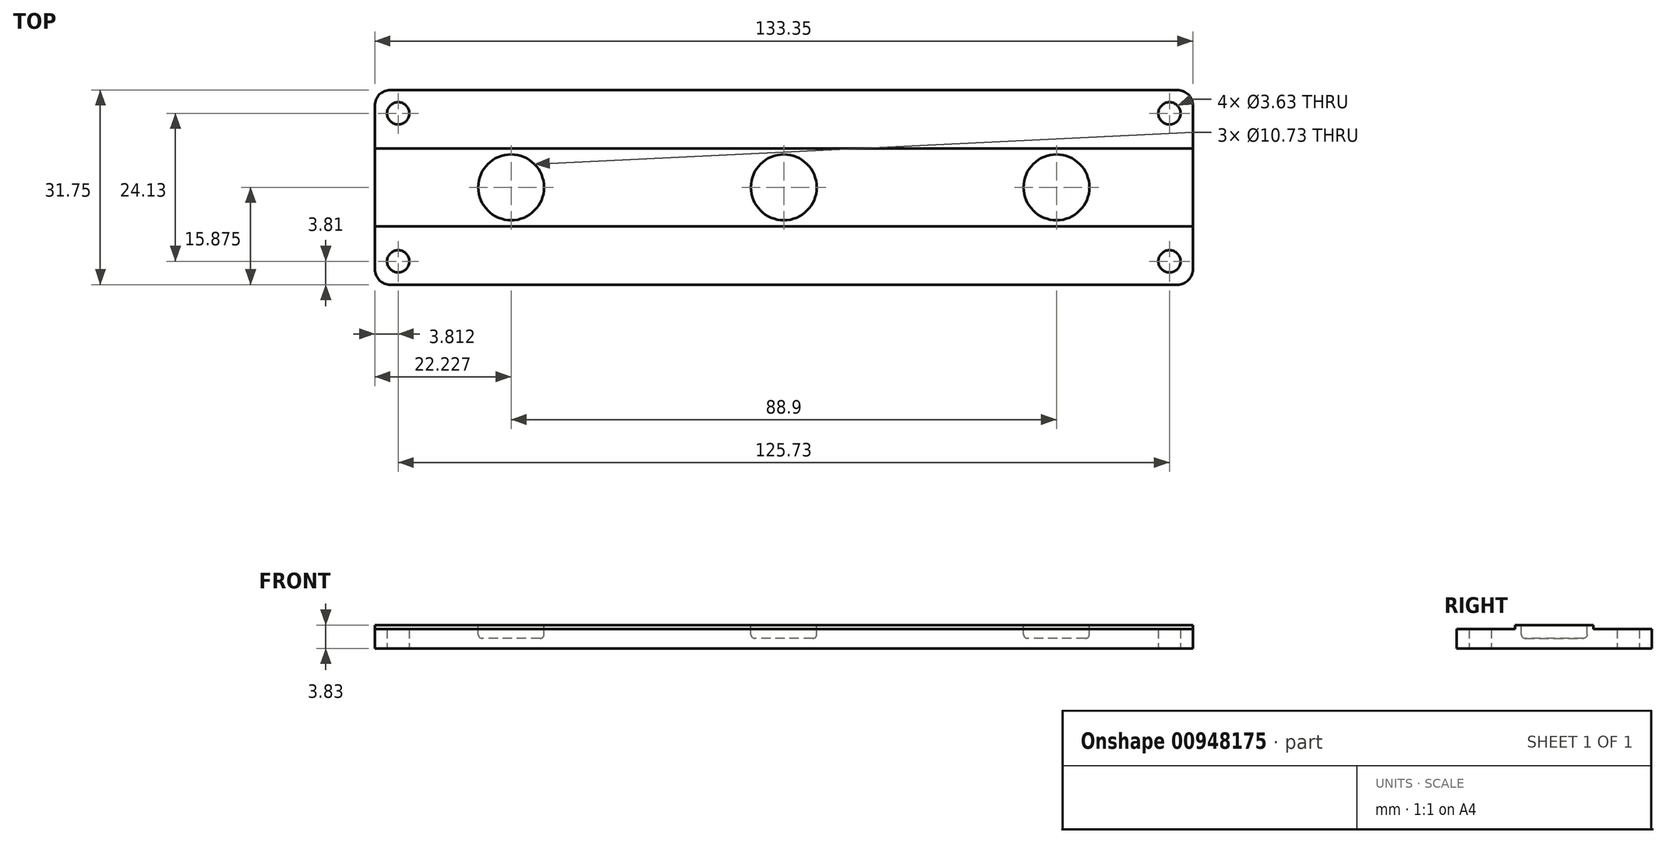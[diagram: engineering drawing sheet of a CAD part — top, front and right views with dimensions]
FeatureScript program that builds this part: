
annotation { "Feature Type Name" : "Feature", "Feature Type Description" : "" }
export const myFeature = defineFeature(function(context is Context, id is Id, definition is map)
    precondition{}
    {
        {
            var Q0;
            Q0=qCreatedBy(makeId("Top.planeOp"),FACE);
            var sketch = newSketch(context, id + "F0", { "sketchPlane" : qUnion([Q0])});
            skLineSegment(sketch, "E0.bottom", {"start": v(51.88, 0) * mm, "end": v(-81.47, 0) * mm});
            skLineSegment(sketch, "E0.top", {"start": v(51.88, -31.75) * mm, "end": v(-81.47, -31.75) * mm});
            skLineSegment(sketch, "E0.left", {"start": v(51.88, 0) * mm, "end": v(51.88, -31.75) * mm});
            skLineSegment(sketch, "E0.right", {"start": v(-81.47, 0) * mm, "end": v(-81.47, -31.75) * mm});
            skCircle(sketch, "E1", {"center": v(-77.66, -27.94) * mm, "radius": 1.82 * mm});
            skLineSegment(sketch, "E2", {"start": v(-81.47, -15.88) * mm, "end": v(51.88, -15.88) * mm, "construction": true});
            skLineSegment(sketch, "E3", {"start": v(-14.8, -31.75) * mm, "end": v(-14.8, 0) * mm, "construction": true});
            skCircle(sketch, "E4.MirrorC", {"center": v(-77.66, -3.81) * mm, "radius": 1.82 * mm});
            skCircle(sketch, "E5.MirrorC", {"center": v(48.07, -27.94) * mm, "radius": 1.82 * mm});
            skCircle(sketch, "E6.MirrorC", {"center": v(48.07, -3.8) * mm, "radius": 1.82 * mm});
            skLineSegment(sketch, "E7.left", {"start": v(-81.47, -8.22) * mm, "end": v(-81.47, -24.11) * mm});
            skLineSegment(sketch, "E7.right", {"start": v(51.88, -8.22) * mm, "end": v(51.88, -24.11) * mm});
            skSolve(sketch);
        }
        {
            var Q0;
            Q0=makeQuery(id+"F0.imprint","IMPRINT",FACE,{"disambiguationData":[TD([[makeQuery(id+"F0.imprint","IMPRINT",EDGE,{"derivedFrom":sQuery(id+"F0.wireOp",EDGE,"E0.bottom")}),1.0]])]});
            extrude(context, id + "F1", {"entities" : qUnion([Q0]), "depth" : 3.17 * mm, "offsetDistance" : 25.4 * mm});
        }
        {
            var Q0;
            Q0=makeQuery(id+"F1.opExtrude","CAP_FACE",FACE,{"disambiguationData":[OSD([sQuery(id+"F0.wireOp",EDGE,"E0.bottom"),sQuery(id+"F0.wireOp",EDGE,"E0.top"),sQuery(id+"F0.wireOp",EDGE,"E0.left"),sQuery(id+"F0.wireOp",EDGE,"E0.right"),sQuery(id+"F0.wireOp",EDGE,"E1"),sQuery(id+"F0.wireOp",EDGE,"E4.MirrorC"),sQuery(id+"F0.wireOp",EDGE,"E5.MirrorC"),sQuery(id+"F0.wireOp",EDGE,"E6.MirrorC"),sQuery(id+"F0.wireOp",EDGE,"E7.left"),sQuery(id+"F0.wireOp",EDGE,"E7.right")])],"isStart":false});
            var sketch = newSketch(context, id + "F2", { "sketchPlane" : qUnion([Q0])});
            skLineSegment(sketch, "E8", {"start": v(-81.47, 0) * mm, "end": v(51.88, -31.75) * mm, "construction": true});
            skLineSegment(sketch, "E9", {"start": v(-81.47, -31.75) * mm, "end": v(51.88, 0) * mm, "construction": true});
            skLineSegment(sketch, "E10.bottom", {"start": v(51.88, -22.23) * mm, "end": v(-81.47, -22.23) * mm});
            skLineSegment(sketch, "E10.top", {"start": v(51.88, -9.53) * mm, "end": v(-81.47, -9.53) * mm});
            skLineSegment(sketch, "E10.left", {"start": v(51.88, -22.23) * mm, "end": v(51.88, -9.53) * mm});
            skLineSegment(sketch, "E10.right", {"start": v(-81.47, -22.23) * mm, "end": v(-81.47, -9.53) * mm});
            skPoint(sketch, "E10.middle", {"position": v(-14.8, -15.88) * mm});
            skSolve(sketch);
        }
        {
            var Q0;
            Q0=makeQuery(id+"F2.imprint","IMPRINT",FACE,{"disambiguationData":[TD([[makeQuery(id+"F2.imprint","IMPRINT",EDGE,{"derivedFrom":sQuery(id+"F2.wireOp",EDGE,"E10.bottom")}),-1.0]])]});
            extrude(context, id + "F3", {"entities" : qUnion([Q0]), "operationType" : NewBodyOperationType.ADD, "depth" : (.125 + (.85 - .32)) * mm, "offsetDistance" : 25.4 * mm});
        }
        {
            var Q0;
            Q0=makeQuery(id+"F3.opExtrude","CAP_FACE",FACE,{"disambiguationData":[OSD([sQuery(id+"F2.wireOp",EDGE,"E10.bottom"),sQuery(id+"F2.wireOp",EDGE,"E10.top"),sQuery(id+"F2.wireOp",EDGE,"E10.left"),sQuery(id+"F2.wireOp",EDGE,"E10.right")])],"isStart":false});
            var sketch = newSketch(context, id + "F4", { "sketchPlane" : qUnion([Q0])});
            skLineSegment(sketch, "E11", {"start": v(-81.47, -15.88) * mm, "end": v(51.88, -15.88) * mm, "construction": true});
            skLineSegment(sketch, "E12", {"start": v(-14.8, -9.53) * mm, "end": v(-14.8, -22.23) * mm, "construction": true});
            skCircle(sketch, "E13", {"center": v(-14.8, -15.88) * mm, "radius": 5.37 * mm});
            skCircle(sketch, "E14", {"center": v(29.66, -15.88) * mm, "radius": 5.37 * mm});
            skCircle(sketch, "E15", {"center": v(-59.24, -15.88) * mm, "radius": 5.37 * mm});
            skCircle(sketch, "E16", {"center": v(-59.24, -15.88) * mm, "radius": 6.35 * mm});
            skCircle(sketch, "E17", {"center": v(-14.8, -15.88) * mm, "radius": 6.35 * mm});
            skCircle(sketch, "E18", {"center": v(29.66, -15.88) * mm, "radius": 6.35 * mm});
            skSolve(sketch);
        }
        {
            var Q0;
            Q0=makeQuery(id+"F4.imprint","IMPRINT",FACE,{"disambiguationData":[TD([[makeQuery(id+"F4.imprint","IMPRINT",EDGE,{"derivedFrom":sQuery(id+"F4.wireOp",EDGE,"E15")}),1.0]])]});
            var Q1;
            Q1=makeQuery(id+"F4.imprint","IMPRINT",FACE,{"disambiguationData":[TD([[makeQuery(id+"F4.imprint","IMPRINT",EDGE,{"derivedFrom":sQuery(id+"F4.wireOp",EDGE,"E13")}),1.0]])]});
            var Q2;
            Q2=makeQuery(id+"F4.imprint","IMPRINT",FACE,{"disambiguationData":[TD([[makeQuery(id+"F4.imprint","IMPRINT",EDGE,{"derivedFrom":sQuery(id+"F4.wireOp",EDGE,"E14")}),1.0]])]});
            extrude(context, id + "F5", {"entities" : qUnion([Q0, Q1, Q2]), "operationType" : NewBodyOperationType.REMOVE, "oppositeDirection" : true, "depth" : 2.16 * mm, "offsetDistance" : 25.4 * mm});
        }
        {
            var Q0;
            Q0=makeQuery(id+"F1.opExtrude","SWEPT_EDGE",EDGE,{"disambiguationData":[OSD([sQuery(id+"F0.wireOp",EDGE,"E0.bottom"),sQuery(id+"F0.wireOp",EDGE,"E0.right")])]});
            var Q1;
            Q1=makeQuery(id+"F1.opExtrude","SWEPT_EDGE",EDGE,{"disambiguationData":[OSD([sQuery(id+"F0.wireOp",EDGE,"E0.top"),sQuery(id+"F0.wireOp",EDGE,"E0.right")])]});
            var Q2;
            Q2=makeQuery(id+"F1.opExtrude","SWEPT_EDGE",EDGE,{"disambiguationData":[OSD([sQuery(id+"F0.wireOp",EDGE,"E0.bottom"),sQuery(id+"F0.wireOp",EDGE,"E0.left")])]});
            var Q3;
            Q3=makeQuery(id+"F1.opExtrude","SWEPT_EDGE",EDGE,{"disambiguationData":[OSD([sQuery(id+"F0.wireOp",EDGE,"E0.top"),sQuery(id+"F0.wireOp",EDGE,"E0.left")])]});
            fillet(context, id + "F6", {"entities" : qUnion([Q0, Q1, Q2, Q3]), "radius" : 2.54 * mm, "tangentPropagation" : true, "allowEdgeOverflow" : false});
        }
        {
            var Q0;
            Q0=makeQuery(id+"F5.boolean.opBoolean","COPY",EDGE,{"derivedFrom":makeQuery(id+"F5.opExtrude","CAP_EDGE",EDGE,{"disambiguationData":[OSD([sQuery(id+"F4.wireOp",EDGE,"E15")])],"isStart":false})});
            var Q1;
            Q1=makeQuery(id+"F5.boolean.opBoolean","COPY",EDGE,{"derivedFrom":makeQuery(id+"F5.opExtrude","CAP_EDGE",EDGE,{"disambiguationData":[OSD([sQuery(id+"F4.wireOp",EDGE,"E13")])],"isStart":false})});
            var Q2;
            Q2=makeQuery(id+"F5.boolean.opBoolean","COPY",EDGE,{"derivedFrom":makeQuery(id+"F5.opExtrude","CAP_EDGE",EDGE,{"disambiguationData":[OSD([sQuery(id+"F4.wireOp",EDGE,"E14")])],"isStart":false})});
            fillet(context, id + "F7", {"entities" : qUnion([Q0, Q1, Q2]), "radius" : 0.64 * mm, "tangentPropagation" : true, "allowEdgeOverflow" : false});
        }
    });
